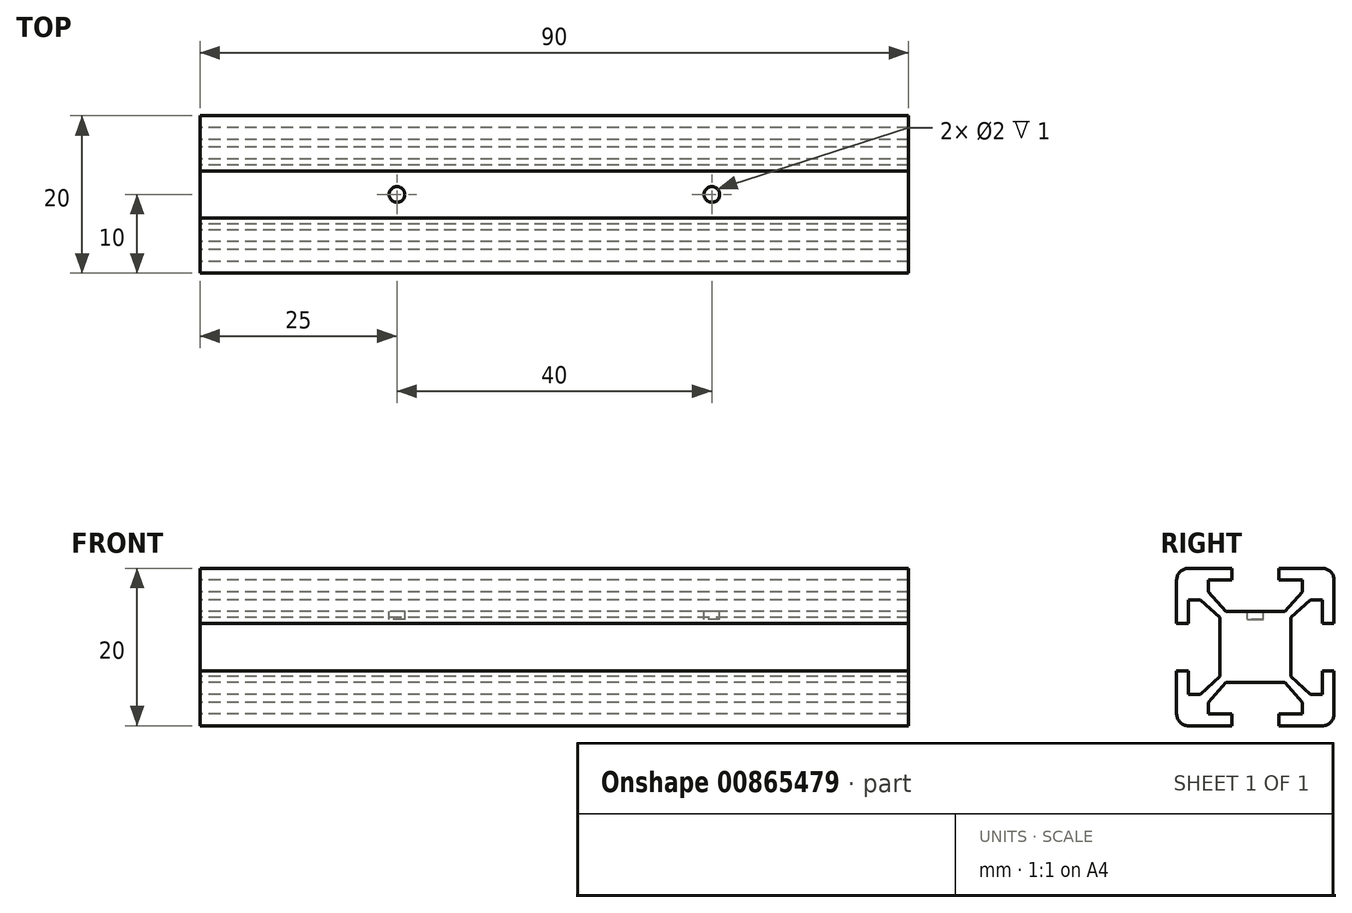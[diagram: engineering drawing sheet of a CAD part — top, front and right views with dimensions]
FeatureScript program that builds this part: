
annotation { "Feature Type Name" : "Feature", "Feature Type Description" : "" }
export const myFeature = defineFeature(function(context is Context, id is Id, definition is map)
    precondition{}
    {
        {
            var Q0;
            Q0=qCreatedBy(makeId("Right.planeOp"),FACE);
            var sketch = newSketch(context, id + "F0", { "sketchPlane" : qUnion([Q0])});
            skLineSegment(sketch, "E0.bottom", {"start": v(8.5, 10) * mm, "end": v(3, 10) * mm});
            skLineSegment(sketch, "E0.top", {"start": v(8.5, -10) * mm, "end": v(-8.5, -10) * mm});
            skLineSegment(sketch, "E0.left", {"start": v(10, 8.5) * mm, "end": v(10, 3) * mm});
            skLineSegment(sketch, "E0.right", {"start": v(-10, 8.5) * mm, "end": v(-10, 3) * mm});
            skPoint(sketch, "E0.middle", {"position": v(0, 0) * mm});
            skPoint(sketch, "E1.visualSharp", {"position": v(-10, 10) * mm});
            skArc(sketch, "E1.filletArc", {"start": v(-8.5, 10) * mm, "mid": v(-9.56, 9.56) * mm, "end": v(-10, 8.5) * mm});
            skPoint(sketch, "E2.visualSharp", {"position": v(10, 10) * mm});
            skArc(sketch, "E2.filletArc", {"start": v(10, 8.5) * mm, "mid": v(9.56, 9.56) * mm, "end": v(8.5, 10) * mm});
            skPoint(sketch, "E3.visualSharp", {"position": v(10, -10) * mm});
            skArc(sketch, "E3.filletArc", {"start": v(8.5, -10) * mm, "mid": v(9.56, -9.56) * mm, "end": v(10, -8.5) * mm});
            skPoint(sketch, "E4.visualSharp", {"position": v(-10, -10) * mm});
            skArc(sketch, "E4.filletArc", {"start": v(-10, -8.5) * mm, "mid": v(-9.56, -9.56) * mm, "end": v(-8.5, -10) * mm});
            skLineSegment(sketch, "E5", {"start": v(-3, 10) * mm, "end": v(-3, 8.5) * mm});
            skLineSegment(sketch, "E6", {"start": v(-3, 8.5) * mm, "end": v(-6, 8.5) * mm});
            skLineSegment(sketch, "E7", {"start": v(-6, 8.5) * mm, "end": v(-6, 7) * mm});
            skLineSegment(sketch, "E8", {"start": v(-6, 7) * mm, "end": v(-3.75, 4.5) * mm});
            skLineSegment(sketch, "E9", {"start": v(-3.75, 4.5) * mm, "end": v(0, 4.5) * mm});
            skLineSegment(sketch, "E10.MirrorCS", {"start": v(3, 10) * mm, "end": v(3, 8.5) * mm});
            skLineSegment(sketch, "E11.MirrorCS", {"start": v(3, 8.5) * mm, "end": v(6, 8.5) * mm});
            skLineSegment(sketch, "E12.MirrorCS", {"start": v(6, 8.5) * mm, "end": v(6, 7) * mm});
            skLineSegment(sketch, "E13.MirrorCS", {"start": v(6, 7) * mm, "end": v(3.75, 4.5) * mm});
            skLineSegment(sketch, "E14.MirrorCS", {"start": v(3.75, 4.5) * mm, "end": v(0, 4.5) * mm});
            skLineSegment(sketch, "E15.trimOffspring", {"start": v(-3, 10) * mm, "end": v(-8.5, 10) * mm});
            skLineSegment(sketch, "E16.1.0", {"start": v(-8.5, -3) * mm, "end": v(-8.5, -6) * mm});
            skLineSegment(sketch, "E16.1.1", {"start": v(-8.5, -6) * mm, "end": v(-7, -6) * mm});
            skLineSegment(sketch, "E16.1.2", {"start": v(-7, -6) * mm, "end": v(-4.5, -3.75) * mm});
            skLineSegment(sketch, "E16.1.3", {"start": v(-4.5, -3.75) * mm, "end": v(-4.5, 0) * mm});
            skLineSegment(sketch, "E16.1.4", {"start": v(-4.5, 3.75) * mm, "end": v(-4.5, 0) * mm});
            skLineSegment(sketch, "E16.1.5", {"start": v(-7, 6) * mm, "end": v(-4.5, 3.75) * mm});
            skLineSegment(sketch, "E16.1.6", {"start": v(-8.5, 6) * mm, "end": v(-7, 6) * mm});
            skLineSegment(sketch, "E16.1.7", {"start": v(-8.5, 3) * mm, "end": v(-8.5, 6) * mm});
            skLineSegment(sketch, "E16.1.8", {"start": v(-10, 3) * mm, "end": v(-8.5, 3) * mm});
            skLineSegment(sketch, "E16.1.9", {"start": v(-10, -3) * mm, "end": v(-8.5, -3) * mm});
            skLineSegment(sketch, "E16.2.0", {"start": v(3, -8.5) * mm, "end": v(6, -8.5) * mm});
            skLineSegment(sketch, "E16.2.1", {"start": v(6, -8.5) * mm, "end": v(6, -7) * mm});
            skLineSegment(sketch, "E16.2.2", {"start": v(6, -7) * mm, "end": v(3.75, -4.5) * mm});
            skLineSegment(sketch, "E16.2.3", {"start": v(3.75, -4.5) * mm, "end": v(0, -4.5) * mm});
            skLineSegment(sketch, "E16.2.4", {"start": v(-3.75, -4.5) * mm, "end": v(0, -4.5) * mm});
            skLineSegment(sketch, "E16.2.5", {"start": v(-6, -7) * mm, "end": v(-3.75, -4.5) * mm});
            skLineSegment(sketch, "E16.2.6", {"start": v(-6, -8.5) * mm, "end": v(-6, -7) * mm});
            skLineSegment(sketch, "E16.2.7", {"start": v(-3, -8.5) * mm, "end": v(-6, -8.5) * mm});
            skLineSegment(sketch, "E16.2.8", {"start": v(-3, -10) * mm, "end": v(-3, -8.5) * mm});
            skLineSegment(sketch, "E16.2.9", {"start": v(3, -10) * mm, "end": v(3, -8.5) * mm});
            skLineSegment(sketch, "E16.3.0", {"start": v(8.5, 3) * mm, "end": v(8.5, 6) * mm});
            skLineSegment(sketch, "E16.3.1", {"start": v(8.5, 6) * mm, "end": v(7, 6) * mm});
            skLineSegment(sketch, "E16.3.2", {"start": v(7, 6) * mm, "end": v(4.5, 3.75) * mm});
            skLineSegment(sketch, "E16.3.3", {"start": v(4.5, 3.75) * mm, "end": v(4.5, 0) * mm});
            skLineSegment(sketch, "E16.3.4", {"start": v(4.5, -3.75) * mm, "end": v(4.5, 0) * mm});
            skLineSegment(sketch, "E16.3.5", {"start": v(7, -6) * mm, "end": v(4.5, -3.75) * mm});
            skLineSegment(sketch, "E16.3.6", {"start": v(8.5, -6) * mm, "end": v(7, -6) * mm});
            skLineSegment(sketch, "E16.3.7", {"start": v(8.5, -3) * mm, "end": v(8.5, -6) * mm});
            skLineSegment(sketch, "E16.3.8", {"start": v(10, -3) * mm, "end": v(8.5, -3) * mm});
            skLineSegment(sketch, "E16.3.9", {"start": v(10, 3) * mm, "end": v(8.5, 3) * mm});
            skLineSegment(sketch, "E17.trimOffspring", {"start": v(-10, -3) * mm, "end": v(-10, -8.5) * mm});
            skLineSegment(sketch, "E18.trimOffspring", {"start": v(10, -3) * mm, "end": v(10, -8.5) * mm});
            skSolve(sketch);
        }
        {
            var Q0;
            Q0=makeQuery(id+"F0.imprint","IMPRINT",FACE,{"disambiguationData":[TD([[makeQuery(id+"F0.imprint","IMPRINT",EDGE,{"derivedFrom":sQuery(id+"F0.wireOp",EDGE,"E0.bottom")}),1.0]])]});
            extrude(context, id + "F1", {"entities" : qUnion([Q0]), "depth" : 90 * mm, "offsetDistance" : 25 * mm});
        }
        {
            var Q0;
            Q0=makeQuery(id+"F1.opExtrude","SWEPT_FACE",FACE,{"disambiguationData":[OSD([sQuery(id+"F0.wireOp",EDGE,"E9"),sQuery(id+"F0.wireOp",EDGE,"E14.MirrorCS")])]});
            var sketch = newSketch(context, id + "F2", { "sketchPlane" : qUnion([Q0])});
            skCircle(sketch, "E19", {"center": v(65, 0) * mm, "radius": 1 * mm});
            skCircle(sketch, "E20", {"center": v(25, 0) * mm, "radius": 1 * mm});
            skSolve(sketch);
        }
        {
            var Q0;
            Q0 = qSketchRegion(id + "F2", true);
            extrude(context, id + "F3", {"entities" : qUnion([Q0]), "operationType" : NewBodyOperationType.REMOVE, "oppositeDirection" : true, "depth" : 1 * mm, "offsetDistance" : 25 * mm});
        }
    });
